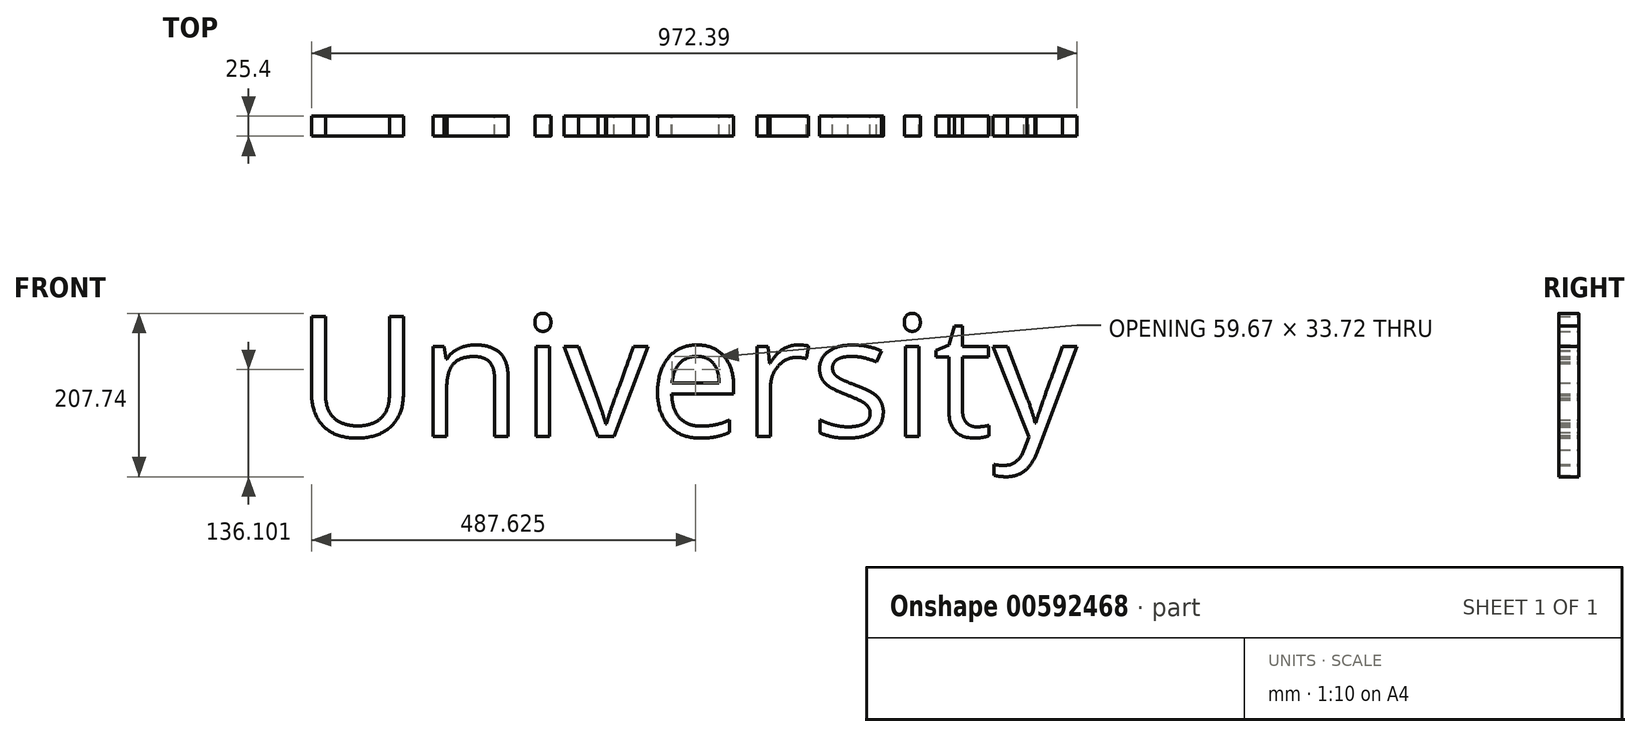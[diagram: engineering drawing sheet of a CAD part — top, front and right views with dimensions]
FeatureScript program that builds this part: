
annotation { "Feature Type Name" : "Feature", "Feature Type Description" : "" }
export const myFeature = defineFeature(function(context is Context, id is Id, definition is map)
    precondition{}
    {
        {
            var Q0;
            Q0=qCreatedBy(makeId("Front.planeOp"),FACE);
            var sketch = newSketch(context, id + "F0", { "sketchPlane" : qUnion([Q0])});
            skText(sketch, "E0", { "text": "University", "fontName": "OpenSans-Regular.ttf"});
            const initialGuessF0  = {"E0": [-0.07528, -0.07667, 1, 0, 0.15353]};
            skSetInitialGuess(sketch, initialGuessF0);
            skSolve(sketch);
        }
        {
            var Q0;
            Q0 = qSketchRegion(id + "F0", true);
            extrude(context, id + "F1", {"entities" : qUnion([Q0]), "depth" : 25.4 * mm, "offsetDistance" : 25.4 * mm});
        }
    });
